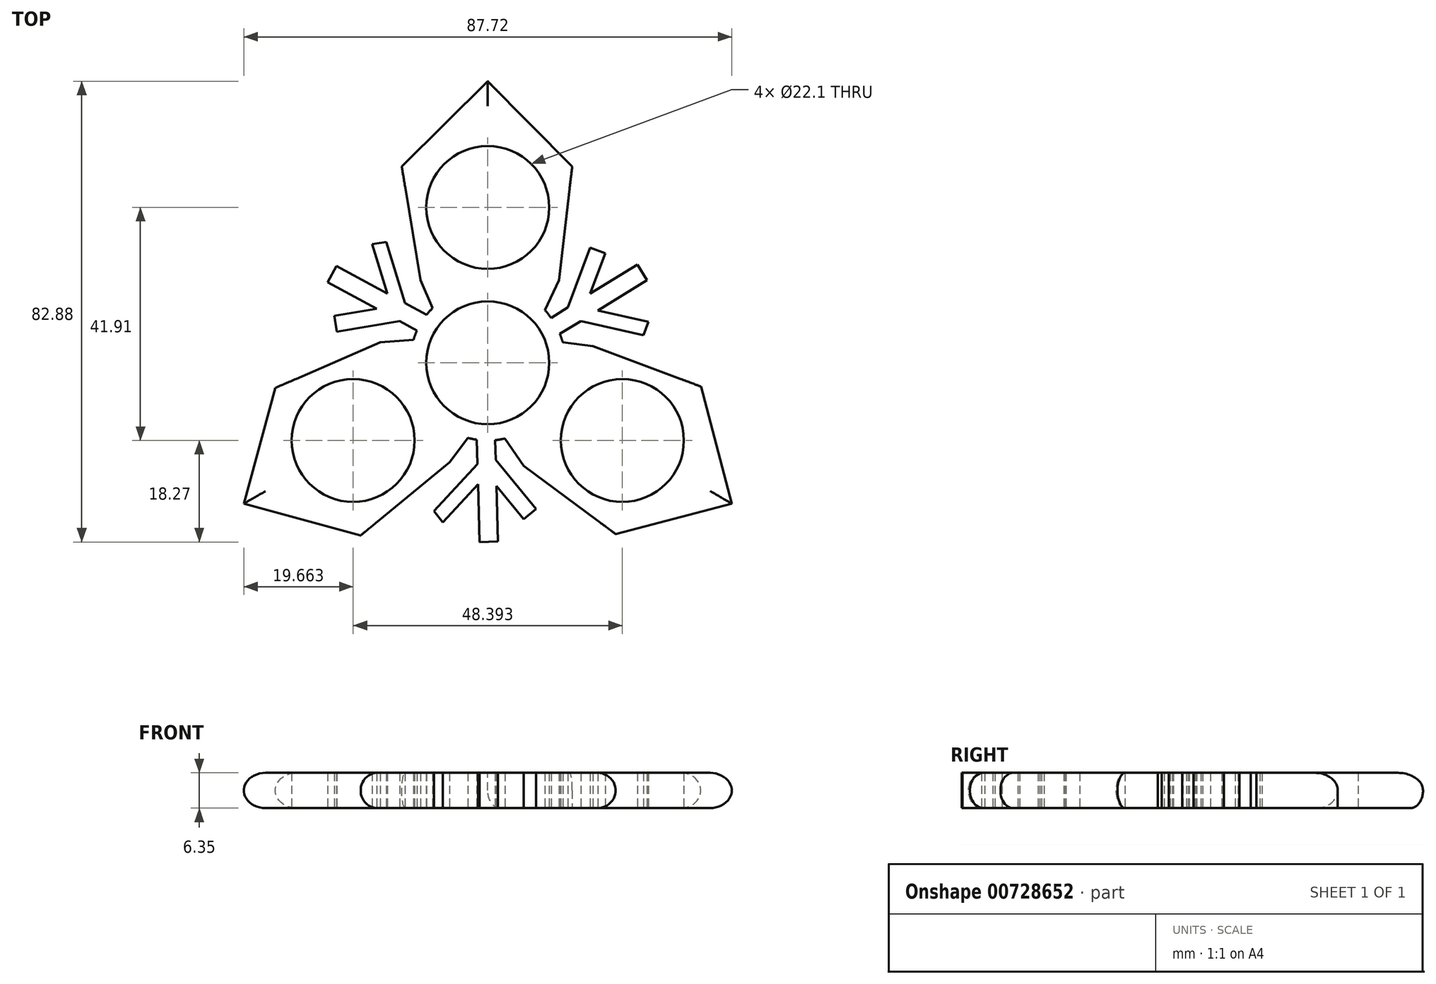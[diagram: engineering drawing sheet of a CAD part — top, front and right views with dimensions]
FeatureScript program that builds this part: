
annotation { "Feature Type Name" : "Feature", "Feature Type Description" : "" }
export const myFeature = defineFeature(function(context is Context, id is Id, definition is map)
    precondition{}
    {
        {
            var Q0;
            Q0=qCreatedBy(makeId("Top.planeOp"),FACE);
            var sketch = newSketch(context, id + "F0", { "sketchPlane" : qUnion([Q0])});
            skCircle(sketch, "E0", {"center": v(0, 0) * mm, "radius": 11.05 * mm});
            skLineSegment(sketch, "E1", {"start": v(0, 0) * mm, "end": v(0, 27.94) * mm});
            skCircle(sketch, "E2", {"center": v(0, 27.94) * mm, "radius": 11.05 * mm});
            skCircle(sketch, "E3.1.0", {"center": v(-24.2, -13.97) * mm, "radius": 11.05 * mm});
            skCircle(sketch, "E3.2.0", {"center": v(24.2, -13.97) * mm, "radius": 11.05 * mm});
            skLineSegment(sketch, "E4", {"start": v(0, 50.64) * mm, "end": v(-15.46, 35.32) * mm});
            skLineSegment(sketch, "E5", {"start": v(0, 50.64) * mm, "end": v(15.18, 35.32) * mm});
            skLineSegment(sketch, "E6", {"start": v(-15.46, 35.32) * mm, "end": v(-12.06, 14.9) * mm});
            skLineSegment(sketch, "E7", {"start": v(15.18, 35.32) * mm, "end": v(12.83, 14.9) * mm});
            skLineSegment(sketch, "E8", {"start": v(-12.06, 14.9) * mm, "end": v(-9.92, 9.84) * mm});
            skLineSegment(sketch, "E9", {"start": v(12.83, 14.9) * mm, "end": v(10.27, 9.47) * mm});
            skLineSegment(sketch, "E10.1.0", {"start": v(-6.87, -17.9) * mm, "end": v(-3.56, -13.5) * mm});
            skLineSegment(sketch, "E10.1.1", {"start": v(-22.86, -31.05) * mm, "end": v(-6.87, -17.9) * mm});
            skLineSegment(sketch, "E10.1.2", {"start": v(-43.86, -25.32) * mm, "end": v(-22.86, -31.05) * mm});
            skLineSegment(sketch, "E10.1.3", {"start": v(-43.86, -25.32) * mm, "end": v(-38.18, -4.52) * mm});
            skLineSegment(sketch, "E10.1.4", {"start": v(-38.18, -4.52) * mm, "end": v(-19.32, 3.67) * mm});
            skLineSegment(sketch, "E10.1.5", {"start": v(-19.32, 3.67) * mm, "end": v(-13.34, 4.15) * mm});
            skLineSegment(sketch, "E10.2.0", {"start": v(18.93, 3) * mm, "end": v(13.48, 3.67) * mm});
            skLineSegment(sketch, "E10.2.1", {"start": v(38.32, -4.27) * mm, "end": v(18.93, 3) * mm});
            skLineSegment(sketch, "E10.2.2", {"start": v(43.86, -25.32) * mm, "end": v(38.32, -4.27) * mm});
            skLineSegment(sketch, "E10.2.3", {"start": v(43.86, -25.32) * mm, "end": v(23, -30.8) * mm});
            skLineSegment(sketch, "E10.2.4", {"start": v(23, -30.8) * mm, "end": v(6.48, -18.56) * mm});
            skLineSegment(sketch, "E10.2.5", {"start": v(6.48, -18.56) * mm, "end": v(3.07, -13.63) * mm});
            skLineSegment(sketch, "E11", {"start": v(11.38, 8.1) * mm, "end": v(14.4, 9.96) * mm});
            skLineSegment(sketch, "E12", {"start": v(12.96, 5.2) * mm, "end": v(16.72, 7.51) * mm});
            skLineSegment(sketch, "E13", {"start": v(14.4, 9.96) * mm, "end": v(18.42, 20.68) * mm});
            skPoint(sketch, "E13.endSnap0", {"position": v(18.42, 12.43) * mm});
            skLineSegment(sketch, "E14", {"start": v(18.42, 12.43) * mm, "end": v(21.13, 19.67) * mm});
            skLineSegment(sketch, "E15", {"start": v(18.42, 20.68) * mm, "end": v(21.13, 19.67) * mm});
            skLineSegment(sketch, "E16.trimOffspring", {"start": v(18.42, 12.43) * mm, "end": v(26.92, 17.67) * mm});
            skLineSegment(sketch, "E17", {"start": v(16.72, 7.51) * mm, "end": v(27.96, 4.95) * mm});
            skLineSegment(sketch, "E18", {"start": v(19.81, 9.42) * mm, "end": v(28.86, 7.35) * mm});
            skPoint(sketch, "E18.endSnap0", {"position": v(22.34, 6.23) * mm});
            skLineSegment(sketch, "E19", {"start": v(27.96, 4.95) * mm, "end": v(28.86, 7.35) * mm});
            skLineSegment(sketch, "E20", {"start": v(18.42, 12.43) * mm, "end": v(18.93, 12.75) * mm});
            skLineSegment(sketch, "E21", {"start": v(28.65, 14.86) * mm, "end": v(26.92, 17.67) * mm});
            skPoint(sketch, "E22.orphan", {"position": v(22.34, 25.1) * mm});
            skPoint(sketch, "E23.orphan", {"position": v(27.95, 18.3) * mm});
            skPoint(sketch, "E24.orphan", {"position": v(33.78, 6.23) * mm});
            skArc(sketch, "E25", {"start": v(11.38, 8.1) * mm, "mid": v(0.33, 13.97) * mm, "end": v(-10.99, 8.63) * mm});
            skPoint(sketch, "E26.orphan", {"position": v(-8.94, 7.52) * mm});
            skPoint(sketch, "E27.orphan", {"position": v(-10.13, 4.42) * mm});
            skPoint(sketch, "E28.orphan", {"position": v(-2.04, -11.5) * mm});
            skPoint(sketch, "E29.orphan", {"position": v(1.24, -10.98) * mm});
            skPoint(sketch, "E30.orphan", {"position": v(10.98, 3.98) * mm});
            skPoint(sketch, "E31.orphan", {"position": v(8.89, 6.56) * mm});
            skLineSegment(sketch, "E32.1.0", {"start": v(-12.7, 5.8) * mm, "end": v(-15.82, 7.5) * mm});
            skLineSegment(sketch, "E32.1.1", {"start": v(-19.98, 9.73) * mm, "end": v(-28.76, 14.48) * mm});
            skLineSegment(sketch, "E32.1.2", {"start": v(-19.98, 9.73) * mm, "end": v(-27.6, 8.46) * mm});
            skLineSegment(sketch, "E32.1.3", {"start": v(-15.82, 7.5) * mm, "end": v(-27.12, 5.6) * mm});
            skLineSegment(sketch, "E32.1.4", {"start": v(-27.12, 5.6) * mm, "end": v(-27.6, 8.46) * mm});
            skLineSegment(sketch, "E32.1.5", {"start": v(-10.99, 8.63) * mm, "end": v(-14.87, 10.72) * mm});
            skLineSegment(sketch, "E32.1.6", {"start": v(-27.2, 17.38) * mm, "end": v(-28.76, 14.48) * mm});
            skLineSegment(sketch, "E32.1.7", {"start": v(-18.06, 12.45) * mm, "end": v(-20.8, 21.32) * mm});
            skLineSegment(sketch, "E32.1.8", {"start": v(-14.87, 10.72) * mm, "end": v(-18.27, 21.74) * mm});
            skLineSegment(sketch, "E32.1.9", {"start": v(-18.27, 21.74) * mm, "end": v(-20.8, 21.32) * mm});
            skLineSegment(sketch, "E32.2.0", {"start": v(1.32, -13.9) * mm, "end": v(1.42, -17.45) * mm});
            skLineSegment(sketch, "E32.2.1", {"start": v(1.56, -22.17) * mm, "end": v(1.84, -32.14) * mm});
            skLineSegment(sketch, "E32.2.2", {"start": v(1.56, -22.17) * mm, "end": v(6.47, -28.13) * mm});
            skLineSegment(sketch, "E32.2.3", {"start": v(1.42, -17.45) * mm, "end": v(8.7, -26.3) * mm});
            skLineSegment(sketch, "E32.2.4", {"start": v(8.7, -26.3) * mm, "end": v(6.47, -28.13) * mm});
            skLineSegment(sketch, "E32.2.5", {"start": v(-1.98, -13.83) * mm, "end": v(-1.85, -18.24) * mm});
            skLineSegment(sketch, "E32.2.6", {"start": v(-1.45, -32.24) * mm, "end": v(1.84, -32.14) * mm});
            skLineSegment(sketch, "E32.2.7", {"start": v(-1.75, -21.87) * mm, "end": v(-8.07, -28.67) * mm});
            skLineSegment(sketch, "E32.2.8", {"start": v(-1.85, -18.24) * mm, "end": v(-9.7, -26.7) * mm});
            skLineSegment(sketch, "E32.2.9", {"start": v(-9.7, -26.7) * mm, "end": v(-8.07, -28.67) * mm});
            skLineSegment(sketch, "E33.trimOffspring", {"start": v(-18.06, 12.45) * mm, "end": v(-27.2, 17.38) * mm});
            skLineSegment(sketch, "E34.trimOffspring", {"start": v(-1.75, -21.87) * mm, "end": v(-1.45, -32.24) * mm});
            skLineSegment(sketch, "E35.trimOffspring", {"start": v(19.81, 9.42) * mm, "end": v(28.65, 14.86) * mm});
            skArc(sketch, "E36.trimOffspring", {"start": v(1.32, -13.9) * mm, "mid": v(11.93, -7.27) * mm, "end": v(12.96, 5.2) * mm});
            skArc(sketch, "E37.trimOffspring", {"start": v(-12.7, 5.8) * mm, "mid": v(-12.26, -6.7) * mm, "end": v(-1.98, -13.83) * mm});
            skSolve(sketch);
        }
        {
            var Q0;
            Q0 = qSketchRegion(id + "F0", true);
            extrude(context, id + "F1", {"entities" : qUnion([Q0]), "depth" : 6.35 * mm, "offsetDistance" : 25.4 * mm});
        }
        {
            var Q0;
            Q0=makeQuery(id+"F1.opExtrude","CAP_EDGE",EDGE,{"disambiguationData":[OSD([sQuery(id+"F0.wireOp",EDGE,"E4")])],"isStart":false});
            var Q1;
            Q1=makeQuery(id+"F1.opExtrude","CAP_EDGE",EDGE,{"disambiguationData":[OSD([sQuery(id+"F0.wireOp",EDGE,"E5")])],"isStart":false});
            var Q2;
            Q2=makeQuery(id+"F1.opExtrude","CAP_EDGE",EDGE,{"disambiguationData":[OSD([sQuery(id+"F0.wireOp",EDGE,"E10.2.2")])],"isStart":false});
            var Q3;
            Q3=makeQuery(id+"F1.opExtrude","CAP_EDGE",EDGE,{"disambiguationData":[OSD([sQuery(id+"F0.wireOp",EDGE,"E10.2.3")])],"isStart":false});
            var Q4;
            Q4=makeQuery(id+"F1.opExtrude","CAP_EDGE",EDGE,{"disambiguationData":[OSD([sQuery(id+"F0.wireOp",EDGE,"E10.1.3")])],"isStart":false});
            var Q5;
            Q5=makeQuery(id+"F1.opExtrude","CAP_EDGE",EDGE,{"disambiguationData":[OSD([sQuery(id+"F0.wireOp",EDGE,"E10.1.2")])],"isStart":false});
            var Q6;
            Q6=makeQuery(id+"F1.opExtrude","CAP_EDGE",EDGE,{"disambiguationData":[OSD([sQuery(id+"F0.wireOp",EDGE,"E10.1.2")])],"isStart":true});
            var Q7;
            Q7=makeQuery(id+"F1.opExtrude","CAP_EDGE",EDGE,{"disambiguationData":[OSD([sQuery(id+"F0.wireOp",EDGE,"E10.1.3")])],"isStart":true});
            var Q8;
            Q8=makeQuery(id+"F1.opExtrude","CAP_EDGE",EDGE,{"disambiguationData":[OSD([sQuery(id+"F0.wireOp",EDGE,"E4")])],"isStart":true});
            var Q9;
            Q9=makeQuery(id+"F1.opExtrude","CAP_EDGE",EDGE,{"disambiguationData":[OSD([sQuery(id+"F0.wireOp",EDGE,"E10.2.2")])],"isStart":true});
            var Q10;
            Q10=makeQuery(id+"F1.opExtrude","CAP_EDGE",EDGE,{"disambiguationData":[OSD([sQuery(id+"F0.wireOp",EDGE,"E10.2.3")])],"isStart":true});
            fillet(context, id + "F2", {"entities" : qUnion([Q0, Q1, Q2, Q3, Q4, Q5, Q6, Q7, Q8, Q9, Q10]), "radius" : 3.17 * mm, "tangentPropagation" : true, "allowEdgeOverflow" : false});
        }
    });
